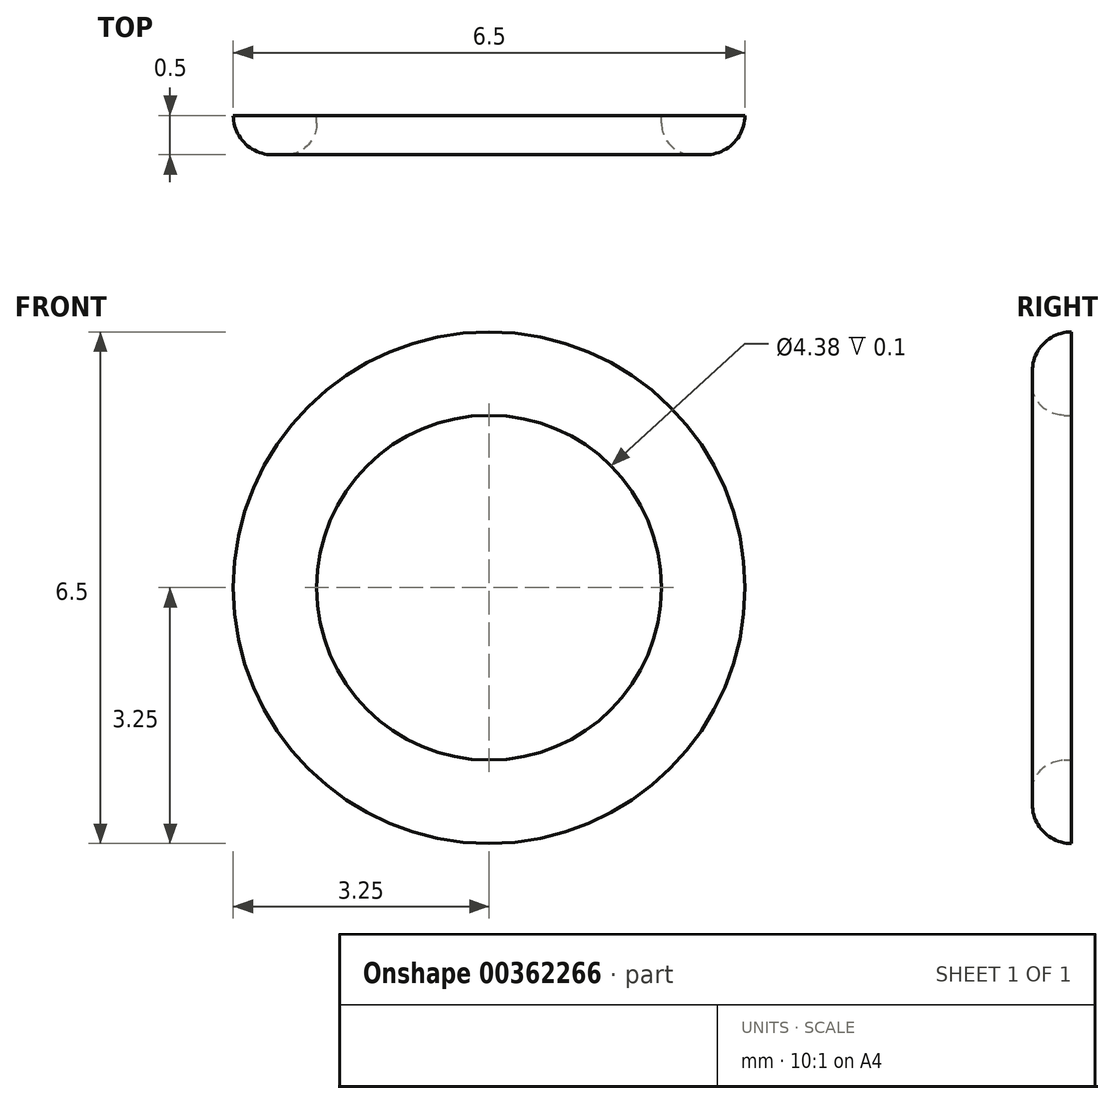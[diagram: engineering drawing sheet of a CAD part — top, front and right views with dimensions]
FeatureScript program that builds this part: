
annotation { "Feature Type Name" : "Feature", "Feature Type Description" : "" }
export const myFeature = defineFeature(function(context is Context, id is Id, definition is map)
    precondition{}
    {
        {
            var Q0;
            Q0=qCreatedBy(makeId("Front.planeOp"),FACE);
            var sketch = newSketch(context, id + "F0", { "sketchPlane" : qUnion([Q0])});
            skCircle(sketch, "E0", {"center": v(0, 0) * mm, "radius": 2.19 * mm});
            skCircle(sketch, "E1", {"center": v(0, 0) * mm, "radius": 3.25 * mm});
            skSolve(sketch);
        }
        {
            var Q0;
            Q0=makeQuery(id+"F0.imprint","IMPRINT",FACE,{"disambiguationData":[TD([[makeQuery(id+"F0.imprint","IMPRINT",EDGE,{"derivedFrom":sQuery(id+"F0.wireOp",EDGE,"E0")}),-1.0]])]});
            extrude(context, id + "F1", {"entities" : qUnion([Q0]), "depth" : .5 * mm});
        }
        {
            var Q0;
            Q0=makeQuery(id+"F1.opExtrude","CAP_EDGE",EDGE,{"disambiguationData":[OSD([sQuery(id+"F0.wireOp",EDGE,"E1")])],"isStart":false});
            fillet(context, id + "F2", {"entities" : qUnion([Q0]), "radius" : .5 * mm, "tangentPropagation" : true, "allowEdgeOverflow" : false});
        }
        {
            var Q0;
            Q0=makeQuery(id+"F1.opExtrude","CAP_EDGE",EDGE,{"disambiguationData":[OSD([sQuery(id+"F0.wireOp",EDGE,"E0")])],"isStart":false});
            fillet(context, id + "F3", {"entities" : qUnion([Q0]), "radius" : .4 * mm, "tangentPropagation" : true, "allowEdgeOverflow" : false});
        }
    });
